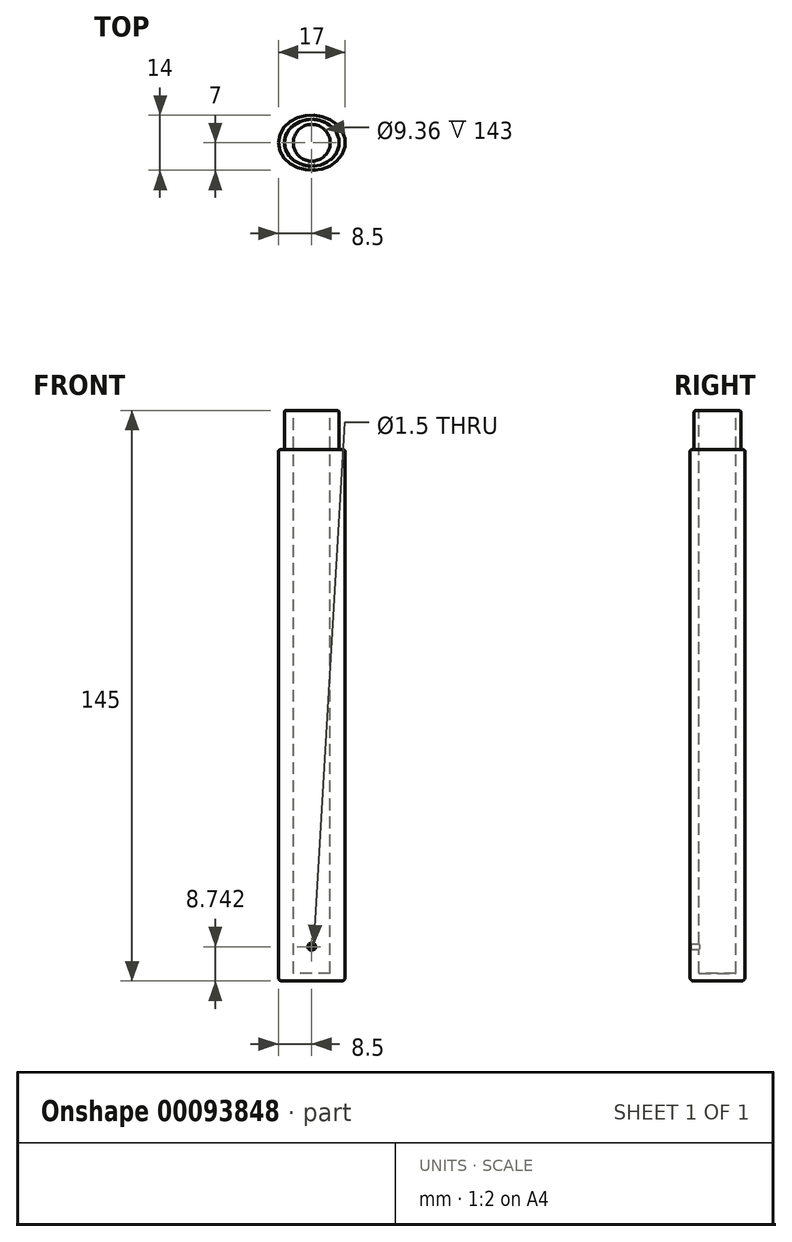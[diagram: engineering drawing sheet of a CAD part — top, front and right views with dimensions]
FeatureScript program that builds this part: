
annotation { "Feature Type Name" : "Feature", "Feature Type Description" : "" }
export const myFeature = defineFeature(function(context is Context, id is Id, definition is map)
    precondition{}
    {
        {
            var Q0;
            Q0=qCreatedBy(makeId("Top.planeOp"),FACE);
            var sketch = newSketch(context, id + "F0", { "sketchPlane" : qUnion([Q0])});
            skEllipse(sketch, "E0", {"center": v(0, 0) * mm, "majorRadius": 8.5 * mm, "minorRadius": 7 * mm, "majorAxis": v(-1, 0)});
            skCircle(sketch, "E1", {"center": v(0, 0) * mm, "radius": 4.55 * mm});
            skSolve(sketch);
        }
        {
            var Q0;
            Q0=qSketchRegion(id+"F0",true);
            var Q1;
            Q1=makeQuery(id+"F0.imprint","IMPRINT",FACE,{"disambiguationData":[TD([[makeQuery(id+"F0.imprint","IMPRINT",EDGE,{"derivedFrom":sQuery(id+"F0.wireOp",EDGE,"E1")}),1.0]])]});
            extrude(context, id + "F1", {"entities" : qUnion([Q0, Q1]), "depth" : 135 * mm});
        }
        {
            var Q0;
            Q0=makeQuery(id+"F1.opExtrude","CAP_FACE",FACE,{"disambiguationData":[OSD([sQuery(id+"F0.wireOp",EDGE,"E0")])],"isStart":false});
            var sketch = newSketch(context, id + "F2", { "sketchPlane" : qUnion([Q0])});
            skEllipse(sketch, "E2", {"center": v(0, 0) * mm, "majorRadius": 6.95 * mm, "minorRadius": 5.95 * mm, "majorAxis": v(-1, 0)});
            skSolve(sketch);
        }
        {
            var Q0;
            Q0=makeQuery(id+"F2.imprint","IMPRINT",FACE,{"disambiguationData":[TD([[makeQuery(id+"F2.imprint","IMPRINT",EDGE,{"derivedFrom":sQuery(id+"F2.wireOp",EDGE,"E2")}),1.0]])]});
            extrude(context, id + "F3", {"entities" : qUnion([Q0]), "operationType" : NewBodyOperationType.ADD, "depth" : 10 * mm});
        }
        {
            var Q0;
            Q0=makeQuery(id+"F3.opExtrude","CAP_FACE",FACE,{"disambiguationData":[OSD([sQuery(id+"F2.wireOp",EDGE,"E2")])],"isStart":false});
            var sketch = newSketch(context, id + "F4", { "sketchPlane" : qUnion([Q0])});
            skCircle(sketch, "E3", {"center": v(0, 0) * mm, "radius": 4.68 * mm});
            skSolve(sketch);
        }
        {
            var Q0;
            Q0=makeQuery(id+"F4.imprint","IMPRINT",FACE,{"disambiguationData":[TD([[makeQuery(id+"F4.imprint","IMPRINT",EDGE,{"derivedFrom":sQuery(id+"F4.wireOp",EDGE,"E3")}),1.0]])]});
            extrude(context, id + "F5", {"entities" : qUnion([Q0]), "operationType" : NewBodyOperationType.REMOVE, "oppositeDirection" : true, "depth" : 143 * mm});
        }
        {
            var Q0;
            Q0=makeQuery(id+"F5.boolean.opBoolean","COPY",EDGE,{"derivedFrom":makeQuery(id+"F5.opExtrude","CAP_EDGE",EDGE,{"disambiguationData":[OSD([sQuery(id+"F4.wireOp",EDGE,"E3")])],"isStart":true})});
            var Q1;
            Q1=makeQuery(id+"F3.opExtrude","CAP_EDGE",EDGE,{"disambiguationData":[OSD([sQuery(id+"F2.wireOp",EDGE,"E2")])],"isStart":false});
            var Q2;
            Q2=makeQuery(id+"F1.opExtrude","CAP_EDGE",EDGE,{"disambiguationData":[OSD([sQuery(id+"F0.wireOp",EDGE,"E0")])],"isStart":false});
            fillet(context, id + "F6", {"entities" : qUnion([Q0, Q1, Q2]), "radius" : .5 * mm, "tangentPropagation" : true, "allowEdgeOverflow" : false});
        }
        {
            var Q0;
            Q0=makeQuery(id+"F1.opExtrude","CAP_EDGE",EDGE,{"disambiguationData":[OSD([sQuery(id+"F0.wireOp",EDGE,"E0")])],"isStart":true});
            fillet(context, id + "F7", {"entities" : qUnion([Q0]), "radius" : 1 * mm, "tangentPropagation" : true, "allowEdgeOverflow" : false});
        }
        {
            var Q0;
            Q0=qCreatedBy(makeId("Front.planeOp"),FACE);
            var sketch = newSketch(context, id + "F8", { "sketchPlane" : qUnion([Q0])});
            skCircle(sketch, "E4", {"center": v(0, 8.74) * mm, "radius": 0.75 * mm});
            skSolve(sketch);
        }
        {
            var Q0;
            Q0=qSketchRegion(id+"F8",true);
            extrude(context, id + "F9", {"entities" : qUnion([Q0]), "operationType" : NewBodyOperationType.REMOVE, "depth" : 25 * mm});
        }
        {
            var Q0;
            Q0=makeQuery(id+"F9.boolean.opBoolean","INTERSECT",EDGE,{"derivedFrom":[makeQuery(id+"F1.opExtrude","SWEPT_FACE",FACE,{"disambiguationData":[OSD([sQuery(id+"F0.wireOp",EDGE,"E0")])]}),makeQuery(id+"F9.opExtrude","SWEPT_FACE",FACE,{"disambiguationData":[OSD([sQuery(id+"F8.wireOp",EDGE,"E4")])]})]});
            fillet(context, id + "F10", {"entities" : qUnion([Q0]), "radius" : .2 * mm, "tangentPropagation" : true, "allowEdgeOverflow" : false});
        }
    });
